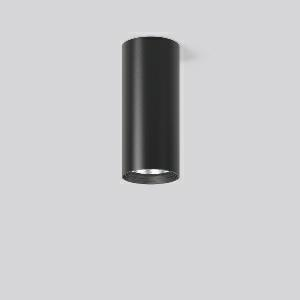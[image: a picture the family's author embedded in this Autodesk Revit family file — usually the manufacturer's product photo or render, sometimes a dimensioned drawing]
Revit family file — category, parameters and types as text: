
# Revit family: heledon_mini_a_931201_003_3_37cb
name_source: partatom
category: Lighting Fixtures
units: mm (PartAtom-declared; Revit-internal decimal feet)

## family parameters
Cut with Voids When Loaded = No
Host = Face
Light Source = No
Part Type = Normal
Room Calculation Point = No
Round Connector Dimension = Use Diameter
Shared = No

## types (1)
- HELEDON mini A (1 x LED Modul 935, 2500 lm, 3500)
    Apparent Load = 20 VA
    Approval mark = CE
    CIE Flux Codes = 99 100 100 100 100
    Color Rendering = 92
    Color Temperature = 3500
    Default Elevation = 1800 mm
    Description = Series: HELEDON mini
Cylindrical surface-mounted downlight. Housing: die-cast aluminium, powder-coated. Internal ceiling frame polycarbonate with bayonet mounting. Black plastic ring and recessed LED to prevent glare from the side. Optical assembly with reflector made of MIRO-Silver with 98% total light reflection for outstanding efficiency - can be changed without tools. Best colour rendering index Ra>90. Suitable for Ceiling mounting. Easy installation with a separate ceiling frame with bayonet mounting and plug connection. Driver integrated. Connected via plug-in connector. High quality converter without flickering and stroboscopic effect. The following accessories can be mounted without use of tools: interchangeable lenses, decorative glasses, honeycomb louvre, clear and frosted diffusers, white interchangeable plastic ring. 
Colour: deep black, matt (RAL 9005)
Diameter: 87 mm
Height: 197 mm
Lamp: LED
Socket: without socket
Colour temperature: 3500K
Colour rendering index (CRI): 92
System power: 20 W
Rated luminous flux: 2500 lm
Luminous efficiency: 125 lm/W
Control gear: Regulated power supply
Protection class: I
Type of protection: IP 20
    Height = 197 mm
    Lamp = 1 x LED Modul 935
    Lamp Light Flux = 2500 lm
    Lamp count = 1
    Length = 87 mm
    Lifetime = 50000 h
    Luminous efficacy = 125 lm/W
    Manufacturer = RZB
    ModVariant = No
    Model = 931201.003.3
    Mounting Place = Ceiling
    Mounting Type = Surface mounted
    Number of Poles = 1
    OnlyDefault = Yes
    Power Factor = 1
    Product Name = HELEDON mini A
    Product group = Surface mounted downlights
    ProductGroupID = 302
    Protection Class = Protection class I
    Protection Degree = IP 20
    RLX_Detail_Level = 1
    RLX_Emergency_Light_Flux = 0 lm
    RLX_Emergency_Type = 0
    RLX_Emergency_Type_DB = No
    RlxData = <blob elided: 106957 chars, md5=8775e0f9>
    Socket = socket
    Standby Power = 0 W
    System Light Flux = 2500 lm
    System Power = 20 W
    Type Comments = Product without accessories
    Type Image = 931188.003.jpg
    URL = http://relux.com
    VarID = ---
    Voltage = 230 V
    Voltage Range = 220-240 V
    Weight = 0.00 kg
    Width = 0 mm  [stored 0 ft]

note: [stored X ft] marks values corroborated as IEEE doubles in the binary element streams (Revit-internal decimal feet)

## geometry (parser evidence)
native form markers: Blend x4, Sweep x10
no freeform markers — native parametric forms only
